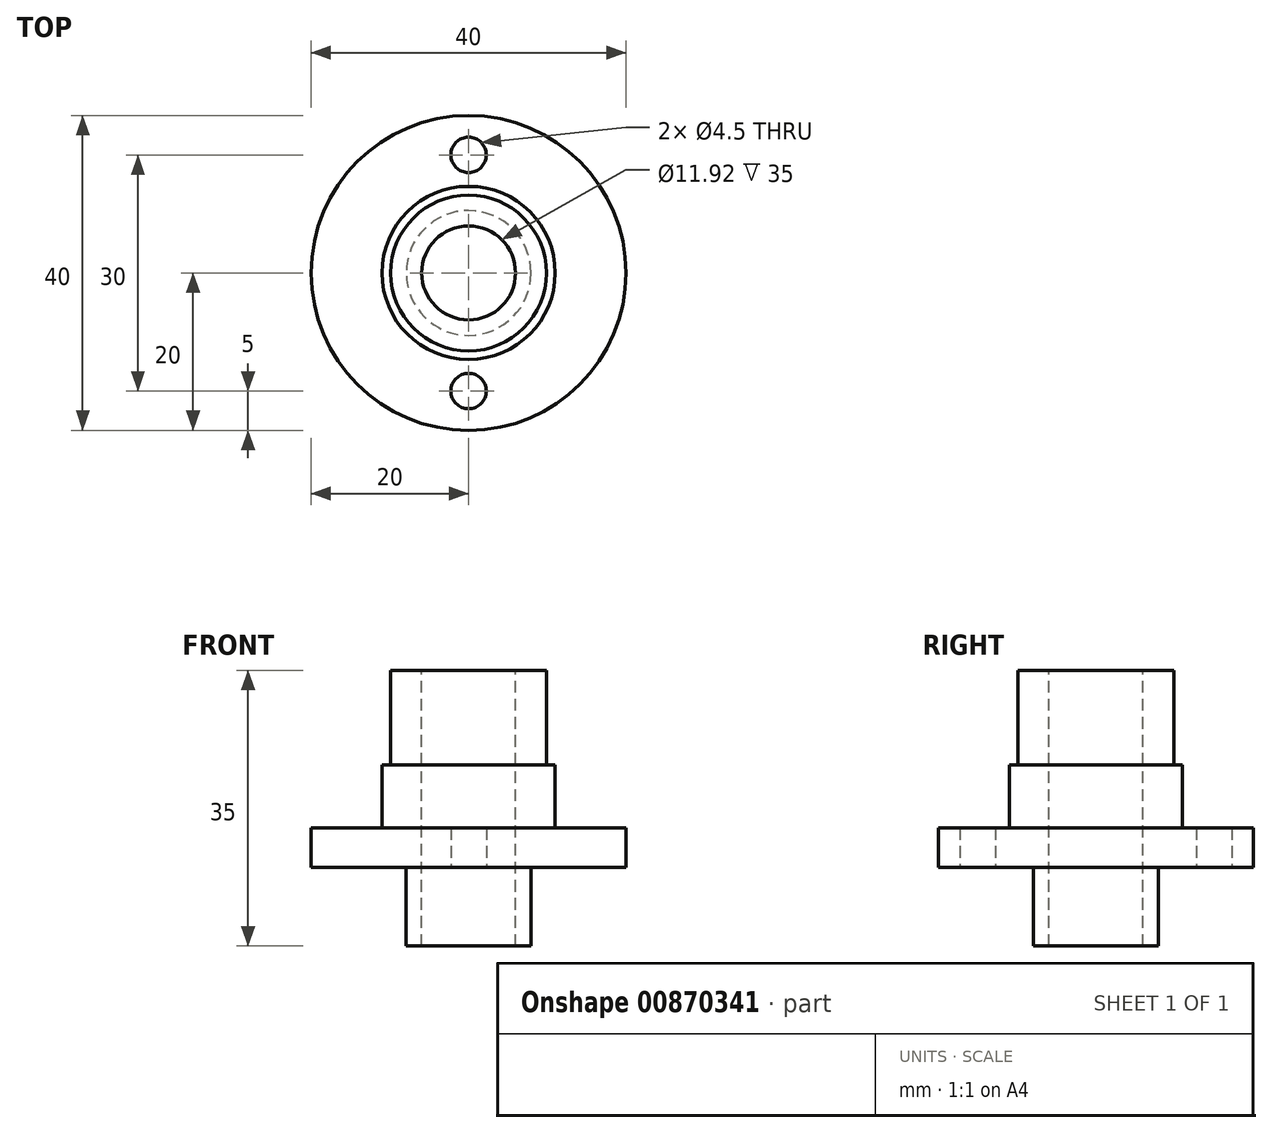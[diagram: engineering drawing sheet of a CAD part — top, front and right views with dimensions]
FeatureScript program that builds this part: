
annotation { "Feature Type Name" : "Feature", "Feature Type Description" : "" }
export const myFeature = defineFeature(function(context is Context, id is Id, definition is map)
    precondition{}
    {
        {
            var Q0;
            Q0=qCreatedBy(makeId("Top.planeOp"),FACE);
            var sketch = newSketch(context, id + "F0", { "sketchPlane" : qUnion([Q0])});
            skCircle(sketch, "E0", {"center": v(0, 0) * mm, "radius": 20 * mm});
            skSolve(sketch);
        }
        {
            var Q0;
            Q0 = qSketchRegion(id + "F0", true);
            extrude(context, id + "F1", {"entities" : qUnion([Q0]), "depth" : 5 * mm, "offsetDistance" : 25 * mm});
        }
        {
            var Q0;
            Q0=makeQuery(id+"F1.opExtrude","CAP_FACE",FACE,{"disambiguationData":[OSD([sQuery(id+"F0.wireOp",EDGE,"E0")])],"isStart":false});
            var sketch = newSketch(context, id + "F2", { "sketchPlane" : qUnion([Q0])});
            skCircle(sketch, "E1", {"center": v(0, 0) * mm, "radius": 11 * mm});
            skSolve(sketch);
        }
        {
            var Q0;
            Q0 = qSketchRegion(id + "F2", true);
            extrude(context, id + "F3", {"entities" : qUnion([Q0]), "operationType" : NewBodyOperationType.ADD, "depth" : 8 * mm, "offsetDistance" : 25 * mm});
        }
        {
            var Q0;
            Q0=makeQuery(id+"F3.opExtrude","CAP_FACE",FACE,{"disambiguationData":[OSD([sQuery(id+"F2.wireOp",EDGE,"E1")])],"isStart":false});
            var sketch = newSketch(context, id + "F4", { "sketchPlane" : qUnion([Q0])});
            skCircle(sketch, "E2", {"center": v(0, 0) * mm, "radius": 9.9 * mm});
            skSolve(sketch);
        }
        {
            var Q0;
            Q0=makeQuery(id+"F4.imprint","IMPRINT",FACE,{"disambiguationData":[TD([[makeQuery(id+"F4.imprint","IMPRINT",EDGE,{"derivedFrom":sQuery(id+"F4.wireOp",EDGE,"E2")}),1.0]])]});
            extrude(context, id + "F5", {"entities" : qUnion([Q0]), "operationType" : NewBodyOperationType.ADD, "depth" : 12 * mm, "offsetDistance" : 25 * mm});
        }
        {
            var Q0;
            Q0=makeQuery(id+"F1.opExtrude","CAP_FACE",FACE,{"disambiguationData":[OSD([sQuery(id+"F0.wireOp",EDGE,"E0")])],"isStart":true});
            var sketch = newSketch(context, id + "F6", { "sketchPlane" : qUnion([Q0])});
            skCircle(sketch, "E3", {"center": v(0, 0) * mm, "radius": 7.92 * mm});
            skSolve(sketch);
        }
        {
            var Q0;
            Q0=makeQuery(id+"F6.imprint","IMPRINT",FACE,{"disambiguationData":[TD([[makeQuery(id+"F6.imprint","IMPRINT",EDGE,{"derivedFrom":sQuery(id+"F6.wireOp",EDGE,"E3")}),1.0]])]});
            extrude(context, id + "F7", {"entities" : qUnion([Q0]), "operationType" : NewBodyOperationType.ADD, "depth" : 10 * mm, "offsetDistance" : 25 * mm});
        }
        {
            var Q0;
            Q0=makeQuery(id+"F5.opExtrude","CAP_FACE",FACE,{"disambiguationData":[OSD([sQuery(id+"F4.wireOp",EDGE,"E2")])],"isStart":false});
            var sketch = newSketch(context, id + "F8", { "sketchPlane" : qUnion([Q0])});
            skPoint(sketch, "E4", {"position": v(0, 0) * mm});
            skSolve(sketch);
        }
        {
            var Q0;
            Q0=sQuery(id+"F8.wireOp",VERTEX,"E4");
            var Q1;
            Q1=makeQuery(id+"F1.opExtrude","SWEPT_BODY",BODY,{"disambiguationData":[OSD([sQuery(id+"F0.wireOp",EDGE,"E0")])]});
            hole(context, id + "F9", {"style" : HoleStyle.SIMPLE, "endStyle" : HoleEndStyle.THROUGH, "holeDiameter" : 11.92 * mm, "majorDiameter" : 5 * mm, "isTappedThrough" : true, "tappedDepth" : 7.6 * mm, "tapClearance" : 3, "locations" : qUnion([Q0]), "scope" : qUnion([Q1])});
        }
        {
            var Q0;
            Q0=makeQuery(id+"F1.opExtrude","CAP_FACE",FACE,{"disambiguationData":[OSD([sQuery(id+"F0.wireOp",EDGE,"E0")])],"isStart":true});
            var sketch = newSketch(context, id + "F10", { "sketchPlane" : qUnion([Q0])});
            skPoint(sketch, "E5", {"position": v(0, -15) * mm});
            skPoint(sketch, "E6", {"position": v(0, 15) * mm});
            skSolve(sketch);
        }
        {
            var Q0;
            Q0=sQuery(id+"F10.wireOp",VERTEX,"E5");
            var Q1;
            Q1=sQuery(id+"F10.wireOp",VERTEX,"E6");
            var Q2;
            Q2=makeQuery(id+"F1.opExtrude","SWEPT_BODY",BODY,{"disambiguationData":[OSD([sQuery(id+"F0.wireOp",EDGE,"E0")])]});
            hole(context, id + "F11", {"style" : HoleStyle.SIMPLE, "endStyle" : HoleEndStyle.THROUGH, "holeDiameter" : 4.5 * mm, "majorDiameter" : 5 * mm, "isTappedThrough" : true, "tappedDepth" : 7.6 * mm, "tapClearance" : 3, "locations" : qUnion([Q0, Q1]), "scope" : qUnion([Q2])});
        }
    });
